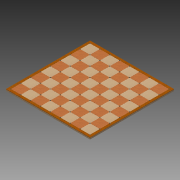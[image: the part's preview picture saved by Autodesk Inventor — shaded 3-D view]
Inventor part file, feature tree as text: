
AUTODESK INVENTOR PART (.ipt)
format: ipt  version: 2013 SP1 (Build 170176100, 176)  size: 961,536 bytes
history: native  units: mm
features: extrude x7, hole x7, pattern_linear x7, sketch x7, other x1
ambient origin geometry x8: Origin, YZ Plane, XZ Plane, XY Plane, X Axis, Y Axis, Z Axis, Center Point
bodies: Volumenkörper4 (feature_tree), Volumenkörper5 (feature_tree), Volumenkörper6 (feature_tree), Volumenkörper7 (feature_tree), Volumenkörper8 (feature_tree), Volumenkörper13 (feature_tree)
feature tree (29):
  extrude  "Extrusion Black"  Depth=1.0mm TaperAngle=0.0deg
  extrude  "Extrusion White"  Depth=1.0mm TaperAngle=0.0deg
  extrude  "Extrusion Kachelleiste unten"  Depth=1.0mm TaperAngle=0.0deg
  extrude  "Extrusion Kachelleiste links"  Depth=1.0mm TaperAngle=0.0deg
  extrude  "Extrusion Kachelleiste oben"  Depth=320.0mm
  extrude  "Extrusion Kachelleiste rechts"  Depth=40.0mm
  hole  "Bohrung2"  [1 undecoded]
  pattern_linear  "Rechteckige Anordnung1"  Count1=4  [1 undecoded]
  hole  "Bohrung3"  [1 undecoded]
  pattern_linear  "Rechteckige Anordnung2"  Count1=4  [1 undecoded]
  hole  "Bohrung4"  [1 undecoded]
  pattern_linear  "Rechteckige Anordnung3"  Count1=4  [1 undecoded]
  hole  "Bohrung5"  [1 undecoded]
  pattern_linear  "Rechteckige Anordnung4"  Count1=4  [1 undecoded]
  hole  "Bohrung6"  [1 undecoded]
  pattern_linear  "Rechteckige Anordnung5"  Count1=4  [1 undecoded]
  hole  "Bohrung7"  [1 undecoded]
  pattern_linear  "Rechteckige Anordnung6"  Count1=4  [1 undecoded]
  extrude  "Extrusion Boden"  Depth=40.0mm
  other  "Körper verschieben Boden"
  hole  "Bohrung Boden"  [1 undecoded]
  pattern_linear  "Rechteckige Anordnung7"  Count1=4  [1 undecoded]
  sketch  "Skizze5"  dims[d531=1.0mm d532=0.0mm d597=1.0mm d598=0.0mm]
  sketch  "Skizze6"  dims[d599=340.0mm d601=1.0mm d602=0.0mm]
  sketch  "Skizze7"  dims[d603=340.0mm d604=1.0mm d605=0.0mm]
  sketch  "Skizze8"  dims[d606=340.0mm d607=1.0mm d608=0.0mm]
  sketch  "Skizze9"  dims[d609=340.0mm d610=320.0mm]
  sketch  "Skizze10"  dims[d611=1.0mm d612=0.0mm d639=40.0mm]
  sketch  "Skizze17"  dims[d640=40.0mm d641=40.0mm d642=40.0mm d643=40.0mm d644=40.0mm d645=40.0mm d646=40.0mm d647=40.0mm d648=40.0mm d649=40.0mm d650=40.0mm d651=40.0mm d652=40.0mm d653=40.0mm d654=40.0mm d655=40.0mm d656=40.0mm d657=40.0mm d658=40.0mm d659=40.0mm d660=40.0mm d661=40.0mm d662=40.0mm d663=40.0mm d664=40.0mm d665=40.0mm d666=40.0mm d667=40.0mm d668=40.0mm d669=40.0mm d670=40.0mm d671=40.0mm d672=40.0mm d673=40.0mm d674=40.0mm d675=40.0mm d676=40.0mm d677=40.0mm d678=40.0mm d679=40.0mm d680=40.0mm d681=40.0mm d682=40.0mm d683=40.0mm d684=40.0mm d685=40.0mm d686=40.0mm d687=40.0mm d688=40.0mm d689=40.0mm d690=40.0mm d691=40.0mm d692=40.0mm d693=40.0mm d694=40.0mm d695=40.0mm d696=40.0mm d697=40.0mm d698=40.0mm d699=40.0mm d700=40.0mm d701=40.0mm d702=40.0mm d703=40.0mm d704=40.0mm d705=40.0mm d706=40.0mm d707=40.0mm d708=40.0mm d709=40.0mm d710=40.0mm d711=40.0mm d712=40.0mm d713=40.0mm d714=40.0mm d715=40.0mm d716=40.0mm d717=40.0mm d718=40.0mm d719=40.0mm d720=40.0mm d721=40.0mm d722=40.0mm d723=40.0mm d724=40.0mm d725=40.0mm d726=40.0mm d727=40.0mm d728=40.0mm d729=40.0mm d730=40.0mm d731=40.0mm d732=40.0mm d733=40.0mm d734=40.0mm d735=40.0mm d736=40.0mm d737=40.0mm d738=40.0mm d739=40.0mm d740=40.0mm d741=40.0mm d742=40.0mm d743=40.0mm d744=40.0mm d745=40.0mm d746=40.0mm d747=40.0mm d748=40.0mm d749=40.0mm d750=40.0mm d751=40.0mm d752=40.0mm d753=40.0mm d754=40.0mm d755=40.0mm d756=40.0mm d757=40.0mm d758=40.0mm d759=40.0mm d760=40.0mm d761=40.0mm d762=40.0mm d763=40.0mm d764=40.0mm d765=40.0mm d766=40.0mm d776=0.0mm d777=0.0mm d778=5.0mm d779=6.0mm d780=4.0mm d781=2.0mm d782=90.0deg d783=12.0mm d784=20.594885mm d785=90.0mm d787=40.0mm d788=90.0mm d790=40.0mm d791=0.0mm d792=0.0mm d793=5.0mm d794=6.0mm d795=4.0mm d796=2.0mm d797=90.0deg d798=12.0mm d799=20.594885mm d800=90.0mm d802=40.0mm d803=90.0mm d805=40.0mm d806=0.0mm d807=0.0mm d808=5.0mm d809=6.0mm d810=4.0mm d811=2.0mm d812=90.0deg d813=12.0mm d814=20.594885mm d815=90.0mm d817=40.0mm d818=0.0mm d819=0.0mm d820=5.0mm d821=6.0mm d822=4.0mm d823=2.0mm d824=90.0deg d825=12.0mm d826=20.594885mm d827=90.0mm d829=40.0mm d830=0.0mm d831=0.0mm d832=5.0mm d833=6.0mm d834=4.0mm d835=2.0mm d836=90.0deg d837=12.0mm d838=20.594885mm d839=90.0mm d841=40.0mm d842=0.0mm d843=0.0mm d844=5.0mm d845=6.0mm d846=4.0mm d847=2.0mm d848=90.0deg d849=12.0mm d850=20.594885mm d851=90.0mm d853=40.0mm d854=6.0mm d855=0.0mm d856=0.0mm d857=0.0mm d858=-1.0mm d859=10.0mm d860=10.0mm d861=5.0mm d862=6.0mm d863=4.0mm d864=2.0mm d865=90.0deg d866=12.0mm d867=20.594885mm d868=90.0mm d870=40.0mm d871=90.0mm d873=40.0mm d600=1.0mm]
note: 14 required parameter values undecoded (feature->parameter linkage not recoverable at this tier; creation-order binding heuristic only, values carry confidence <= 0.55)
